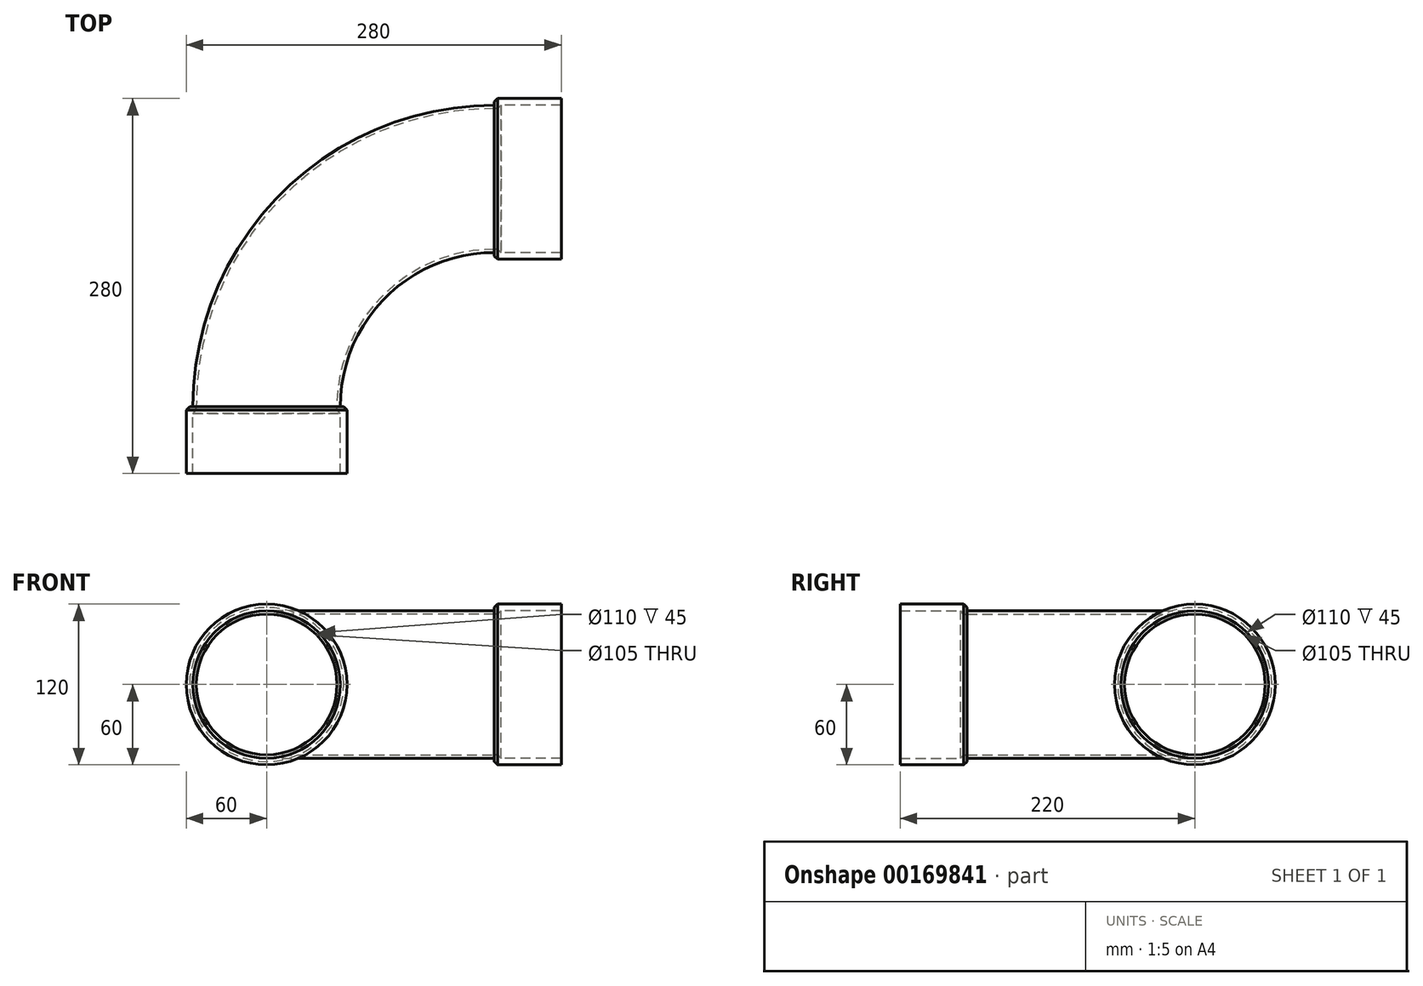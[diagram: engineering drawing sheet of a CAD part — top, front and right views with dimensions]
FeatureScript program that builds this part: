
annotation { "Feature Type Name" : "Feature", "Feature Type Description" : "" }
export const myFeature = defineFeature(function(context is Context, id is Id, definition is map)
    precondition{}
    {
        {
            var Q0;
            Q0=qCreatedBy(makeId("Top.planeOp"),FACE);
            var sketch = newSketch(context, id + "F0", { "sketchPlane" : qUnion([Q0])});
            skArc(sketch, "E0", {"start": v(0, 170) * mm, "mid": v(-120.2, 120.2) * mm, "end": v(-170, 0) * mm});
            skSolve(sketch);
        }
        {
            var Q0;
            Q0=qCreatedBy(makeId("Front.planeOp"),FACE);
            var sketch = newSketch(context, id + "F1", { "sketchPlane" : qUnion([Q0])});
            skCircle(sketch, "E1", {"center": v(-170, 0) * mm, "radius": 55 * mm});
            skSolve(sketch);
        }
        {
            var Q0;
            Q0 = qSketchRegion(id + "F1", true);
            var Q1;
            Q1=sQuery(id+"F0.wireOp",EDGE,"E0");
            sweep(context, id + "F2", {"profiles" : qUnion([Q0]), "path" : qUnion([Q1])});
        }
        {
            var Q0;
            Q0=makeQuery(id+"F2.opSweep","CAP_FACE",FACE,{"disambiguationData":[OSD([sQuery(id+"F0.wireOp",VERTEX,"E0.end"),sQuery(id+"F1.wireOp",EDGE,"E1")])],"isStart":true});
            var Q1;
            Q1=makeQuery(id+"F2.opSweep","CAP_FACE",FACE,{"disambiguationData":[OSD([sQuery(id+"F0.wireOp",VERTEX,"E0.start"),sQuery(id+"F1.wireOp",EDGE,"E1")])],"isStart":false});
            shell(context, id + "F3", {"entities" : qUnion([Q0, Q1]), "thickness" : 2.5 * mm});
        }
        {
            var Q0;
            Q0=makeQuery(id+"F2.opSweep","CAP_FACE",FACE,{"disambiguationData":[OSD([sQuery(id+"F0.wireOp",VERTEX,"E0.end"),sQuery(id+"F1.wireOp",EDGE,"E1")])],"isStart":true});
            var sketch = newSketch(context, id + "F4", { "sketchPlane" : qUnion([Q0])});
            skCircle(sketch, "E2", {"center": v(-170, 0) * mm, "radius": 55 * mm});
            skCircle(sketch, "E3.0", {"center": v(-170, 0) * mm, "radius": 60 * mm});
            skSolve(sketch);
        }
        {
            var Q0;
            Q0 = qSketchRegion(id + "F4", true);
            extrude(context, id + "F5", {"entities" : qUnion([Q0]), "operationType" : NewBodyOperationType.ADD, "depth" : 50 * mm});
        }
        {
            var Q0;
            Q0=makeQuery(id+"F2.opSweep","CAP_FACE",FACE,{"disambiguationData":[OSD([sQuery(id+"F0.wireOp",VERTEX,"E0.end"),sQuery(id+"F1.wireOp",EDGE,"E1")])],"isStart":true});
            extrude(context, id + "F6", {"entities" : qUnion([Q0]), "operationType" : NewBodyOperationType.ADD, "depth" : 5 * mm});
        }
        {
            var Q0;
            Q0=makeQuery(id+"F2.opSweep","CAP_FACE",FACE,{"disambiguationData":[OSD([sQuery(id+"F0.wireOp",VERTEX,"E0.start"),sQuery(id+"F1.wireOp",EDGE,"E1")])],"isStart":false});
            var sketch = newSketch(context, id + "F7", { "sketchPlane" : qUnion([Q0])});
            skCircle(sketch, "E4.0", {"center": v(170, 0) * mm, "radius": 55 * mm});
            skCircle(sketch, "E5.0", {"center": v(170, 0) * mm, "radius": 60 * mm});
            skSolve(sketch);
        }
        {
            var Q0;
            Q0 = qSketchRegion(id + "F7", true);
            extrude(context, id + "F8", {"entities" : qUnion([Q0]), "operationType" : NewBodyOperationType.ADD, "depth" : 50 * mm});
        }
        {
            var Q0;
            Q0=makeQuery(id+"F2.opSweep","CAP_FACE",FACE,{"disambiguationData":[OSD([sQuery(id+"F0.wireOp",VERTEX,"E0.start"),sQuery(id+"F1.wireOp",EDGE,"E1")])],"isStart":false});
            extrude(context, id + "F9", {"entities" : qUnion([Q0]), "operationType" : NewBodyOperationType.ADD, "depth" : 5 * mm});
        }
        {
            var Q0;
            Q0=makeQuery(id+"F5.opExtrude","CAP_EDGE",EDGE,{"disambiguationData":[OSD([sQuery(id+"F4.wireOp",EDGE,"E3.0")])],"isStart":true});
            var Q1;
            {var subQ0=sQuery(id+"F1.wireOp",EDGE,"E1");var subQ1=sQuery(id+"F0.wireOp",VERTEX,"E0.end");Q1=makeQuery(id+"F6.opExtrude","CAP_EDGE",EDGE,{"disambiguationData":[OSD([subQ1,subQ0]),TDD([makeQuery(id+"F3.opShell","OFFSET_EDGE",EDGE,{"disambiguationData":[OSD([subQ1,subQ0])]})])],"isStart":false});}
            var Q2;
            {var subQ0=sQuery(id+"F1.wireOp",EDGE,"E1");var subQ1=sQuery(id+"F0.wireOp",VERTEX,"E0.start");Q2=makeQuery(id+"F9.opExtrude","CAP_EDGE",EDGE,{"disambiguationData":[OSD([subQ1,subQ0]),TDD([makeQuery(id+"F3.opShell","OFFSET_EDGE",EDGE,{"disambiguationData":[OSD([subQ1,subQ0])]})])],"isStart":false});}
            var Q3;
            Q3=makeQuery(id+"F8.opExtrude","CAP_EDGE",EDGE,{"disambiguationData":[OSD([sQuery(id+"F7.wireOp",EDGE,"E5.0")])],"isStart":true});
            chamfer(context, id + "F10", {"entities" : qUnion([Q0, Q1, Q2, Q3]), "width" : 2.5 * mm, "tangentPropagation" : true});
        }
    });
